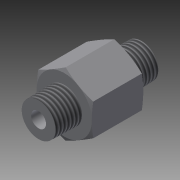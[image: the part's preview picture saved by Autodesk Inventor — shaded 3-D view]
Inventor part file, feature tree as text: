
AUTODESK INVENTOR PART (.ipt)
format: ipt  version: 2018 (Build 220112000, 112)  size: 135,680 bytes
history: native  units: in
note: dims shown in document units (in); Inventor stores cm internally (conversion verified against a paired STEP export)
features: sketch x4, extrude x3, plane x2, thread x2, other x1, hole x1, revolve x1, mirror x1, reference x1
ambient origin geometry x8: Origin, YZ Plane, XZ Plane, XY Plane, X Axis, Y Axis, Z Axis, Center Point
bodies: Solid1 (feature_tree)
feature tree (16):
  sketch  "Sketch1"  dims[d2=0.5in d3=0.0in d20=0.25in d21=-0.0123in]
  extrude  "Extrusion1"  Depth=0.25in
  plane  "Work Plane1"
  other  "Work Axis3"
  extrude  "Extrusion3"  Depth=0.25in
  thread  "Thread2"  [1 undecoded]
  hole  "Hole2"  [1 undecoded]
  extrude  "Extrusion4"  Depth=0.0414in
  thread  "Thread3"  [1 undecoded]
  revolve  "Revolution3"  [1 undecoded]
  plane  "Work Plane4"
  mirror  "Mirror4"
  sketch  "Sketch6"  dims[d22=0.392in d23=0.0in]
  reference  "Reference3"
  sketch  "Sketch7"  dims[d24=0.13in d25=0.75in d26=0.375in d27=0.25in d28=0.5635in d29=1.0in d30=0.8108in d31=0.25in d32=-0.0123in d33=0.392in d34=0.0in]
  sketch  "Sketch8"  dims[d35=90.0deg d36=0.5355in d37=0.0414in d38=0.0415in]
note: 4 required parameter values undecoded (feature->parameter linkage not recoverable at this tier; creation-order binding heuristic only, values carry confidence <= 0.55)
